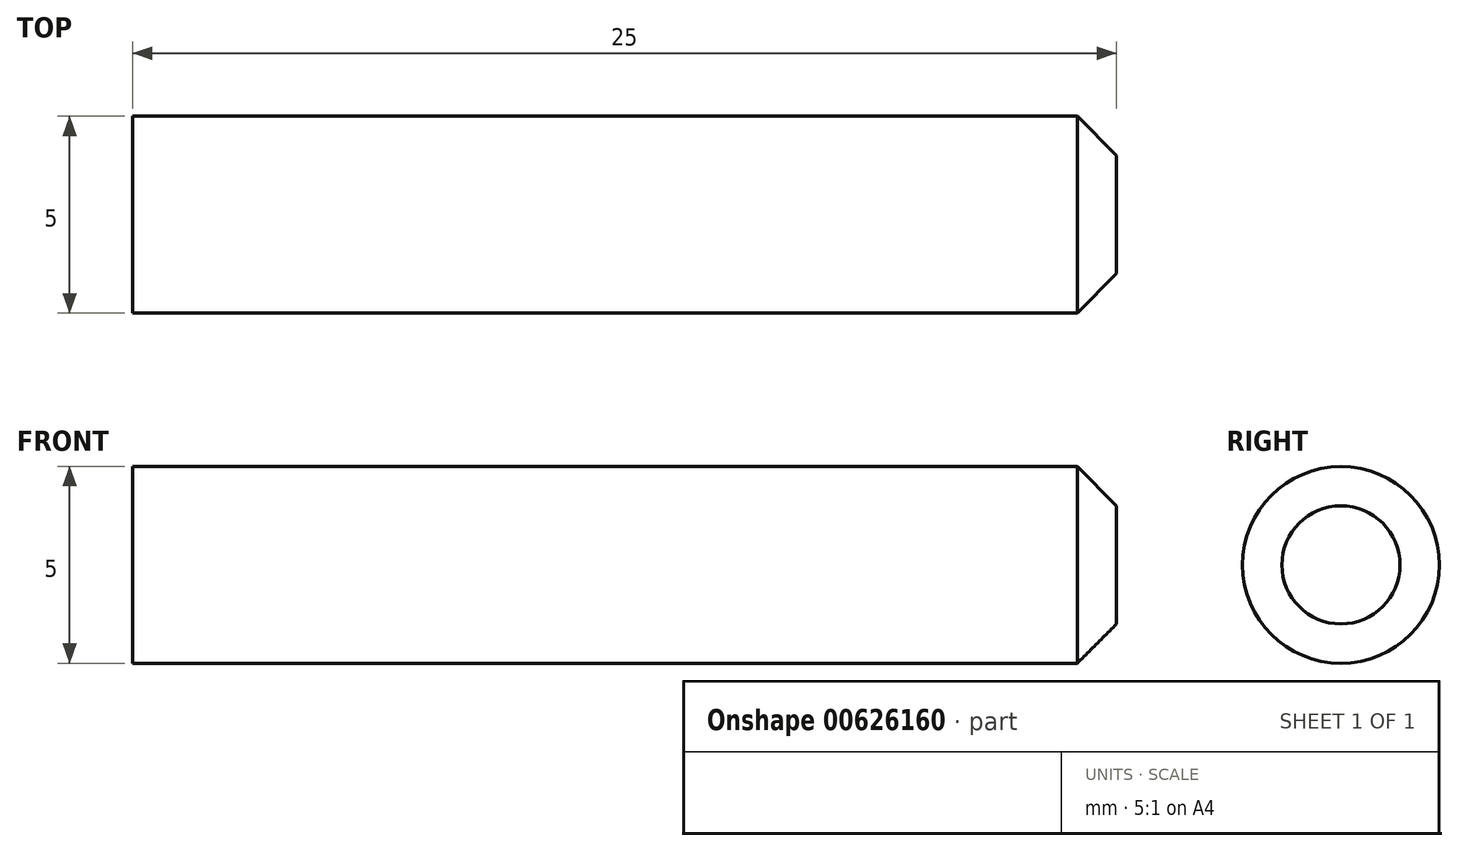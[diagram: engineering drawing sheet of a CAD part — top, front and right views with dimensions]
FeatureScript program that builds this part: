
annotation { "Feature Type Name" : "Feature", "Feature Type Description" : "" }
export const myFeature = defineFeature(function(context is Context, id is Id, definition is map)
    precondition{}
    {
        {
            var Q0;
            Q0=qCreatedBy(makeId("Right.planeOp"),FACE);
            var sketch = newSketch(context, id + "F0", { "sketchPlane" : qUnion([Q0])});
            skCircle(sketch, "E0", {"center": v(0, 0) * mm, "radius": 2.5 * mm});
            skSolve(sketch);
        }
        {
            var Q0;
            Q0 = qSketchRegion(id + "F0", true);
            extrude(context, id + "F1", {"entities" : qUnion([Q0]), "depth" : 25 * mm, "offsetDistance" : 25 * mm});
        }
        {
            var Q0;
            Q0=makeQuery(id+"F1.opExtrude","CAP_EDGE",EDGE,{"disambiguationData":[OSD([sQuery(id+"F0.wireOp",EDGE,"E0")])],"isStart":false});
            chamfer(context, id + "F2", {"entities" : qUnion([Q0]), "width" : 1 * mm, "tangentPropagation" : true});
        }
    });
